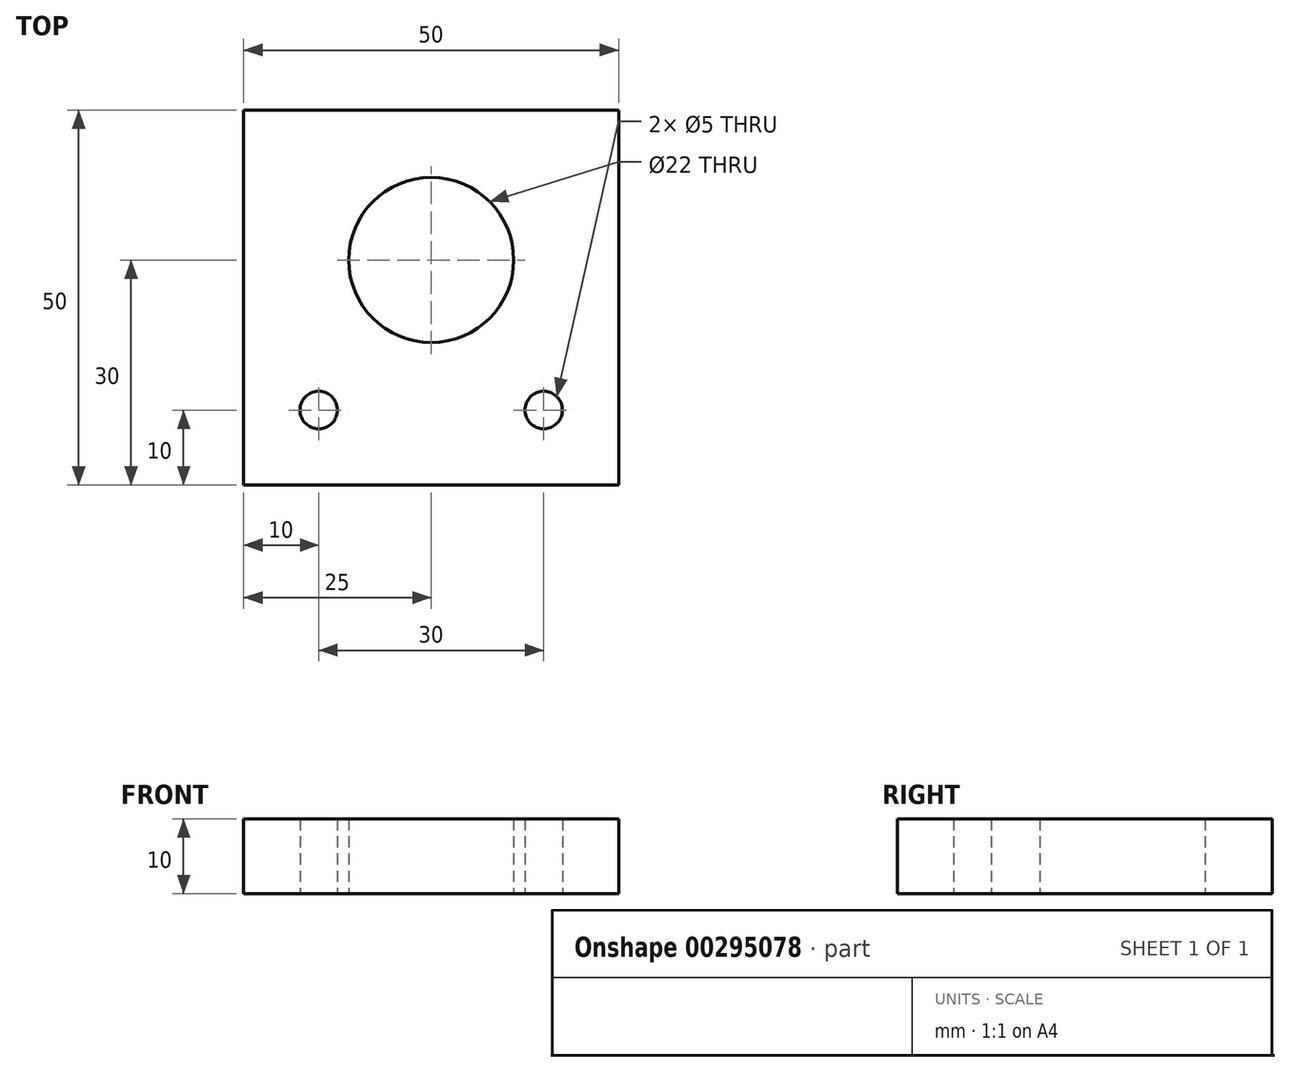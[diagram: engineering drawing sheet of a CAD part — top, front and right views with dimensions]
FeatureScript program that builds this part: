
annotation { "Feature Type Name" : "Feature", "Feature Type Description" : "" }
export const myFeature = defineFeature(function(context is Context, id is Id, definition is map)
    precondition{}
    {
        {
            var Q0;
            Q0=qCreatedBy(makeId("Top.planeOp"),FACE);
            var sketch = newSketch(context, id + "F0", { "sketchPlane" : qUnion([Q0])});
            skLineSegment(sketch, "E0.bottom", {"start": v(25, 25) * mm, "end": v(-25, 25) * mm});
            skLineSegment(sketch, "E0.top", {"start": v(25, -25) * mm, "end": v(-25, -25) * mm});
            skLineSegment(sketch, "E0.left", {"start": v(25, 25) * mm, "end": v(25, -25) * mm});
            skLineSegment(sketch, "E0.right", {"start": v(-25, 25) * mm, "end": v(-25, -25) * mm});
            skPoint(sketch, "E0.middle", {"position": v(0, 0) * mm});
            skCircle(sketch, "E1", {"center": v(0, 5) * mm, "radius": 11 * mm});
            skCircle(sketch, "E2", {"center": v(15, -15) * mm, "radius": 2.5 * mm});
            skCircle(sketch, "E3", {"center": v(-15, -15) * mm, "radius": 2.5 * mm});
            skSolve(sketch);
        }
        {
            var Q0;
            Q0=qSketchRegion(id+"F0",true);
            extrude(context, id + "F1", {"entities" : qUnion([Q0]), "depth" : 10 * mm});
        }
    });
